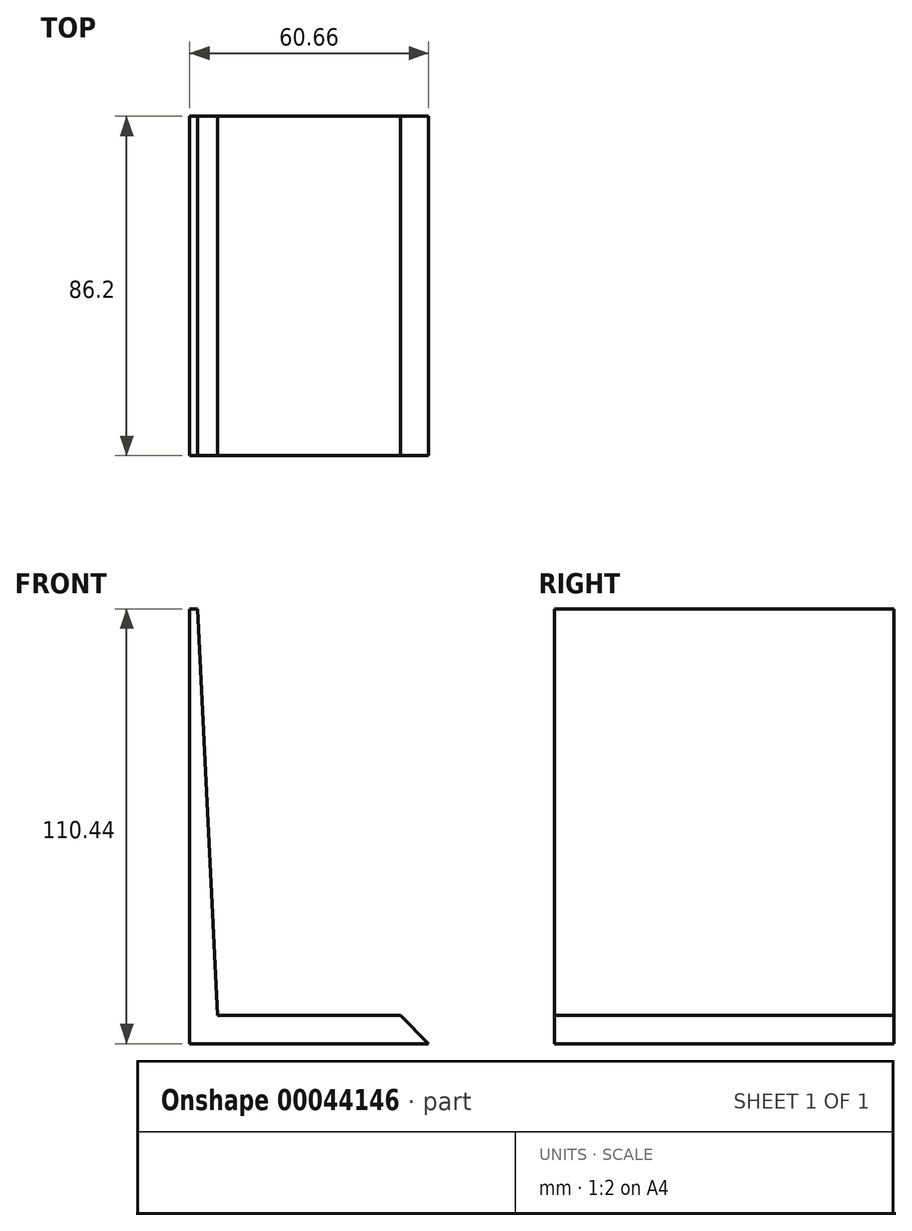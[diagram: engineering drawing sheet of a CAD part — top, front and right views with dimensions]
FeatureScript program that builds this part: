
annotation { "Feature Type Name" : "Feature", "Feature Type Description" : "" }
export const myFeature = defineFeature(function(context is Context, id is Id, definition is map)
    precondition{}
    {
        {
            var Q0;
            Q0=qCreatedBy(makeId("Front.planeOp"),FACE);
            var sketch = newSketch(context, id + "F0", { "sketchPlane" : qUnion([Q0])});
            skLineSegment(sketch, "E0", {"start": v(0, 110.44) * mm, "end": v(0, 0) * mm});
            skLineSegment(sketch, "E1", {"start": v(0, 0) * mm, "end": v(62.42, 0) * mm});
            skLineSegment(sketch, "E2", {"start": v(62.42, 0) * mm, "end": v(62.42, 7.13) * mm});
            skLineSegment(sketch, "E3", {"start": v(62.42, 7.13) * mm, "end": v(7.13, 7.13) * mm});
            skLineSegment(sketch, "E4", {"start": v(7.13, 7.13) * mm, "end": v(7.13, 110.44) * mm});
            skLineSegment(sketch, "E5", {"start": v(7.13, 110.44) * mm, "end": v(0, 110.44) * mm});
            skSolve(sketch);
        }
        {
            var Q0;
            Q0 = qSketchRegion(id + "F0", true);
            extrude(context, id + "F1", {"entities" : qUnion([Q0]), "oppositeDirection" : true, "depth" : 86.2 * mm});
        }
        {
            var Q0;
            Q0=makeQuery(id+"F1.opExtrude","CAP_FACE",FACE,{"disambiguationData":[OSD([sQuery(id+"F0.wireOp",EDGE,"E0"),sQuery(id+"F0.wireOp",EDGE,"E1"),sQuery(id+"F0.wireOp",EDGE,"E2"),sQuery(id+"F0.wireOp",EDGE,"E3"),sQuery(id+"F0.wireOp",EDGE,"E4"),sQuery(id+"F0.wireOp",EDGE,"E5")])],"isStart":true});
            var sketch = newSketch(context, id + "F2", { "sketchPlane" : qUnion([Q0])});
            skLineSegment(sketch, "E6", {"start": v(7.13, 7.13) * mm, "end": v(2.04, 110.44) * mm});
            skLineSegment(sketch, "E7", {"start": v(2.04, 110.44) * mm, "end": v(25.2, 110.44) * mm});
            skLineSegment(sketch, "E8", {"start": v(25.2, 110.44) * mm, "end": v(25.2, 24.27) * mm});
            skLineSegment(sketch, "E9", {"start": v(25.2, 24.27) * mm, "end": v(7.13, 7.13) * mm});
            skSolve(sketch);
        }
        {
            var Q0;
            {var subQ1=sQuery(id+"F2.wireOp",EDGE,"E8");Q0=makeQuery(id+"F2.imprint","IMPRINT",FACE,{"disambiguationData":[TD([[makeQuery(id+"F2.imprint","IMPRINT",EDGE,{"derivedFrom":subQ1}),-1.0]])]});}
            var Q1;
            {var subQ2=sQuery(id+"F2.wireOp",EDGE,"E6");Q1=makeQuery(id+"F2.imprint","IMPRINT",FACE,{"disambiguationData":[TD([[makeQuery(id+"F2.imprint","IMPRINT",EDGE,{"derivedFrom":subQ2}),-1.0]])]});}
            extrude(context, id + "F3", {"entities" : qUnion([Q0, Q1]), "operationType" : NewBodyOperationType.REMOVE, "endBound" : BoundingType.THROUGH_ALL, "oppositeDirection" : true, "depth" : 25.4 * mm});
        }
        {
            var Q0;
            Q0=makeQuery(id+"F1.opExtrude","SWEPT_EDGE",EDGE,{"disambiguationData":[OSD([sQuery(id+"F0.wireOp",EDGE,"E2"),sQuery(id+"F0.wireOp",EDGE,"E3")])]});
            chamfer(context, id + "F4", {"entities" : qUnion([Q0]), "width" : 8.9 * mm, "tangentPropagation" : true});
        }
    });
